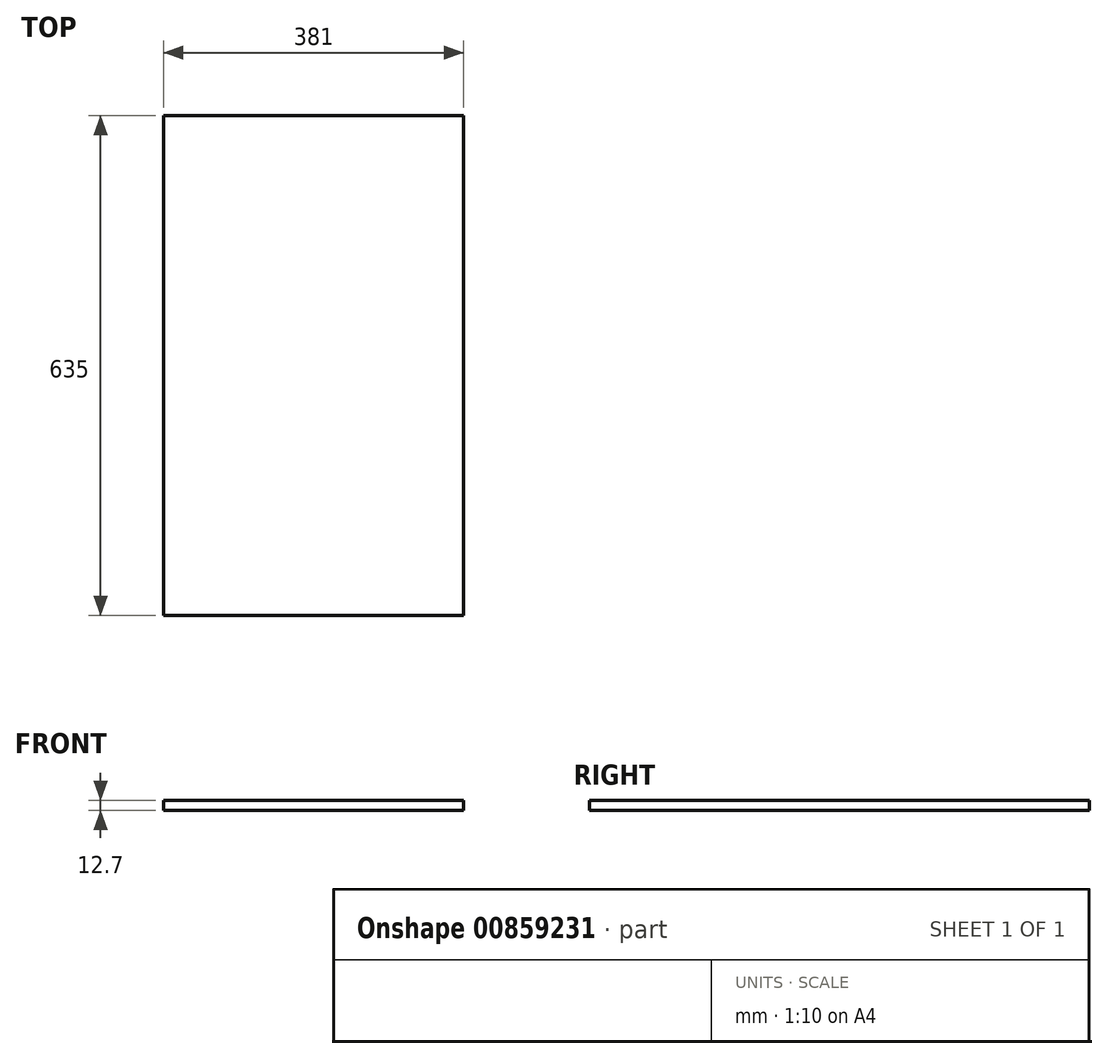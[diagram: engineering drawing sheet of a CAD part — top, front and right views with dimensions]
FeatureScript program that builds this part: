
annotation { "Feature Type Name" : "Feature", "Feature Type Description" : "" }
export const myFeature = defineFeature(function(context is Context, id is Id, definition is map)
    precondition{}
    {
        {
            var Q0;
            Q0=qCreatedBy(makeId("Top.planeOp"),FACE);
            var sketch = newSketch(context, id + "F0", { "sketchPlane" : qUnion([Q0])});
            skLineSegment(sketch, "E0.bottom", {"start": v(0, 0) * mm, "end": v(-381, 0) * mm});
            skLineSegment(sketch, "E0.top", {"start": v(0, 635) * mm, "end": v(-381, 635) * mm});
            skLineSegment(sketch, "E0.left", {"start": v(0, 0) * mm, "end": v(0, 635) * mm});
            skLineSegment(sketch, "E0.right", {"start": v(-381, 0) * mm, "end": v(-381, 635) * mm});
            skSolve(sketch);
        }
        {
            var Q0;
            Q0 = qSketchRegion(id + "F0", true);
            extrude(context, id + "F1", {"entities" : qUnion([Q0]), "depth" : 12.7 * mm, "offsetDistance" : 25.4 * mm});
        }
    });
